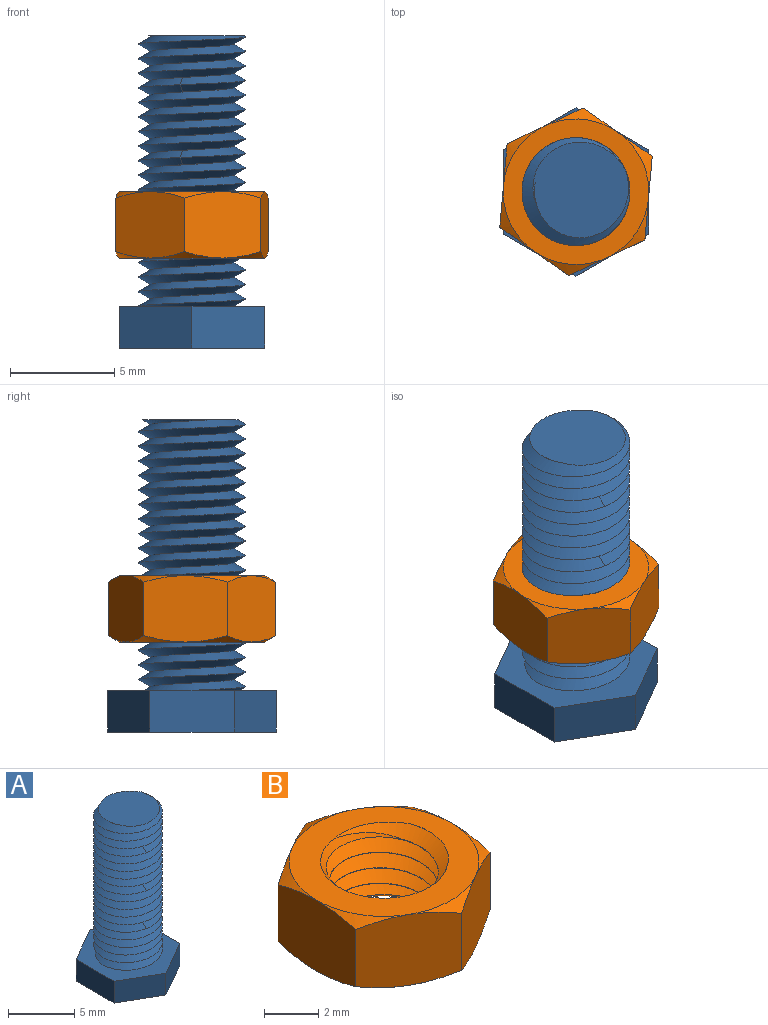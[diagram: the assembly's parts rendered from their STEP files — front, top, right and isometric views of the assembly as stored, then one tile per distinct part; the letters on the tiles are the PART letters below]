
ASSEMBLY  parts=2 mates=1
PART A: 18 faces, bbox 7.5x8.6x15.9 mm
  f0: cylinder r=2mm len=13mm, axis (0,0,-1), area 4.2mm2, adj f1,f2,f3,f4,f5,f6,f7,f8
  f1: plane 5.09x5.09mm, normal (0,0,1), area 16.6mm2, adj f0,f2,f3
  f2: bspline ~5.99x5.19mm, area 35.5mm2, adj f0,f1,f3,f8
  f3: bspline ~5.99x5.19mm, area 30.8mm2, adj f0,f1,f2,f9
  f4: bspline ~5.99x5.19mm, area 54mm2, adj f0,f5,f7,f10
  f5: bspline ~5.99x5.19mm, area 49.4mm2, adj f0,f4,f6,f10
  f6: bspline ~5.99x5.19mm, area 49.5mm2, adj f0,f5,f7,f8
  f7: bspline ~5.99x5.19mm, area 49.5mm2, adj f0,f4,f6,f9
  f8: bspline ~5.99x5.19mm, area 49.5mm2, adj f0,f2,f6,f9
  f9: bspline ~5.99x5.19mm, area 49.5mm2, adj f0,f3,f7,f8
  f10: plane 8.55x7.47mm, normal (0,0,1), area 25.9mm2, adj f0,f4,f5,f11,f12,f13,f14,f15
  f11: plane 4.04x2mm, normal (1,0,0), area 8.1mm2, adj f10,f12,f16,f17
  f12: plane 3.5x2.02mm, normal (0.5,0.87,0), area 8.1mm2, adj f10,f11,f13,f17
  f13: plane 3.5x2.02mm, normal (-0.5,0.87,0), area 8.1mm2, adj f10,f12,f14,f17
  f14: plane 4.04x2mm, normal (-1,0,0), area 8.1mm2, adj f10,f13,f15,f17
  f15: plane 3.5x2.02mm, normal (-0.5,-0.87,0), area 8.1mm2, adj f10,f14,f16,f17
  f16: plane 3.5x2.02mm, normal (0.5,-0.87,0), area 8.1mm2, adj f10,f11,f15,f17
  f17: plane 8.08x7mm, normal (0,0,-1), area 42.4mm2, adj f11,f12,f13,f14,f15,f16
PART B: 25 faces, bbox 8.4x8.4x4.4 mm
  f0: plane 3.83x3.54mm, normal (0.5,-0.87,0), area 12.1mm2, adj f1,f5,f13,f14,f15,f16
  f1: plane 4.38x3.54mm, normal (1,0,0), area 12.1mm2, adj f0,f2,f9,f14,f15,f20
  f2: plane 3.83x3.54mm, normal (0.5,0.87,0), area 12.1mm2, adj f1,f3,f9,f10,f19,f20
  f3: plane 3.83x3.54mm, normal (-0.5,0.87,0), area 12.1mm2, adj f2,f4,f10,f11,f18,f19
  f4: plane 4.38x3.54mm, normal (-1,0,0), area 12.1mm2, adj f3,f5,f11,f12,f17,f18
  f5: plane 3.83x3.54mm, normal (-0.5,-0.87,0), area 12.1mm2, adj f0,f4,f12,f13,f16,f17
  f6: plane 7.12x7.12mm, normal (0,0,-1), area 20.5mm2, adj f15,f16,f17,f18,f19,f20,f22,f23
  f7: plane 7.1x7.1mm, normal (0,0,1), area 20.5mm2, adj f9,f10,f11,f12,f13,f14,f21,f23
  f8: cylinder r=2mm len=4mm, axis (0,0,-1), area 1mm2, adj f21,f22,f23,f24
  f9: cone r=3.5mm half-angle=60deg, axis (0,0,-1), area 1.2mm2, adj f1,f2,f7
  f10: cone r=3.5mm half-angle=60deg, axis (0,0,-1), area 1.2mm2, adj f2,f3,f7
  f11: cone r=3.5mm half-angle=60deg, axis (0,0,-1), area 1.2mm2, adj f3,f4,f7
  f12: cone r=3.5mm half-angle=60deg, axis (0,0,-1), area 1.2mm2, adj f4,f5,f7
  f13: cone r=3.5mm half-angle=60deg, axis (0,0,-1), area 1.2mm2, adj f0,f5,f7
  f14: cone r=3.5mm half-angle=60deg, axis (0,0,-1), area 1.2mm2, adj f0,f1,f7
  f15: cone r=3.5mm half-angle=60deg, axis (0,0,1), area 1.2mm2, adj f0,f1,f6
  f16: cone r=3.5mm half-angle=60deg, axis (0,0,1), area 1.2mm2, adj f0,f5,f6
  f17: cone r=3.5mm half-angle=60deg, axis (0,0,1), area 1.2mm2, adj f4,f5,f6
  f18: cone r=3.5mm half-angle=60deg, axis (0,0,1), area 1.2mm2, adj f3,f4,f6
  f19: cone r=3.5mm half-angle=60deg, axis (0,0,1), area 1.2mm2, adj f2,f3,f6
  f20: cone r=3.5mm half-angle=60deg, axis (0,0,1), area 1.2mm2, adj f1,f2,f6
  f21: cone r=2mm half-angle=45deg, axis (0,0,1), area 2mm2, adj f7,f8,f23,f24
  f22: cone r=2.34mm half-angle=45deg, axis (0,0,-1), area 2mm2, adj f6,f8,f23,f24
  f23: bspline ~5.99x5.19mm, area 42.8mm2, adj f6,f7,f8,f21,f22,f24
  f24: bspline ~5.99x5.19mm, area 42.8mm2, adj f6,f7,f8,f21,f22,f23
PLACE A at identity fixed
PLACE B rot(axis=(0,0,1),115deg) t=(0,0,2.32)mm
MATE cylindrical A.f0 <-> B.f8  axis (0,0,1) through (0,0,0)mm
